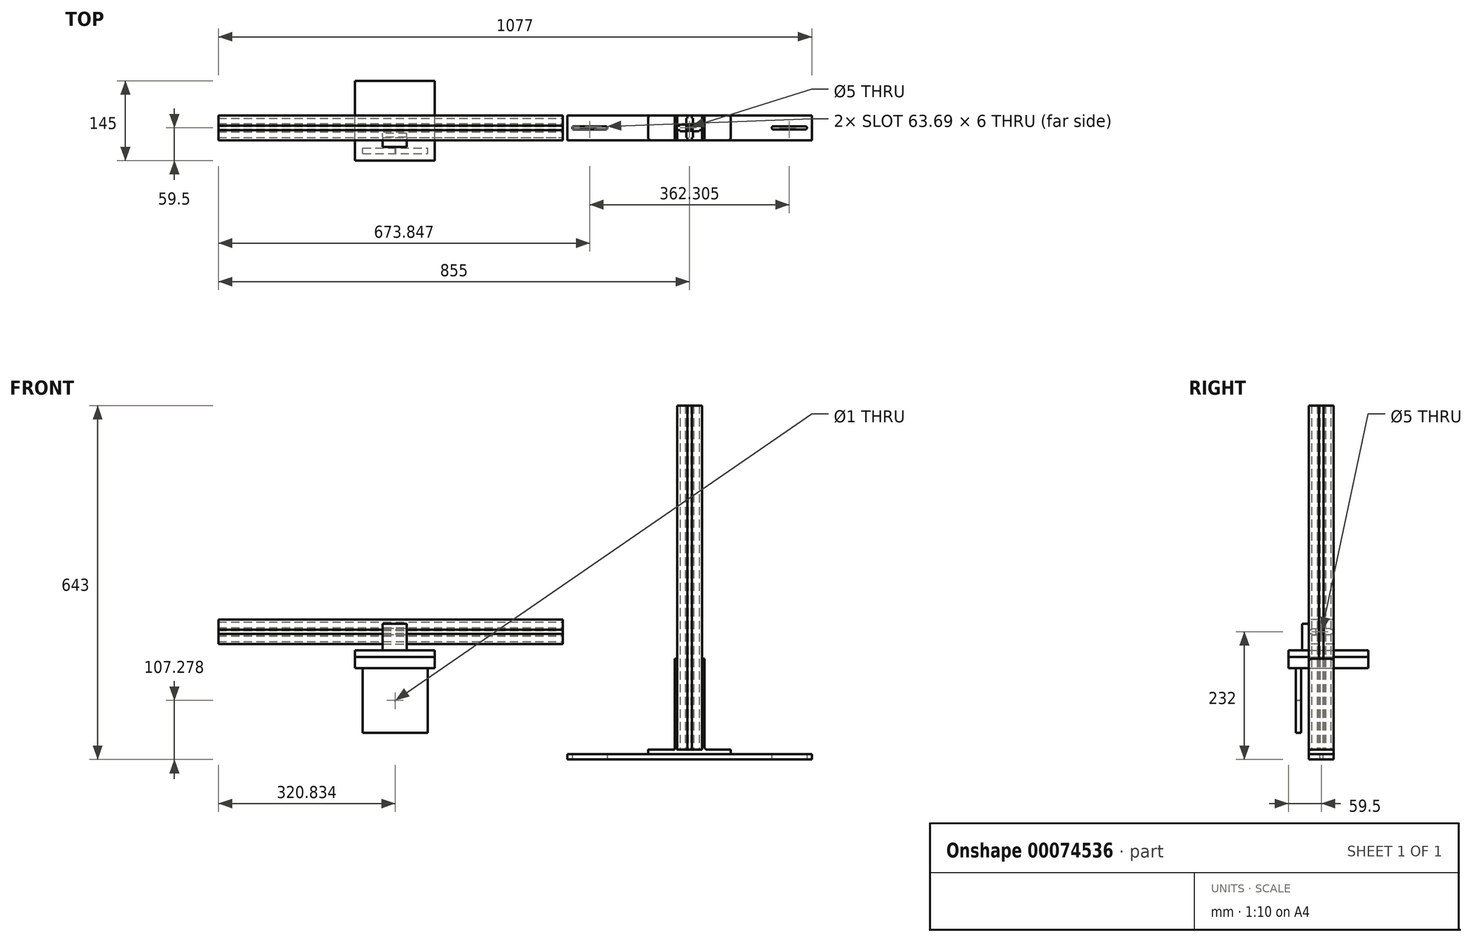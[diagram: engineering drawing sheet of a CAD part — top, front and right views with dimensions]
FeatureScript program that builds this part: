
annotation { "Feature Type Name" : "Feature", "Feature Type Description" : "" }
export const myFeature = defineFeature(function(context is Context, id is Id, definition is map)
    precondition{}
    {
        {
            var Q0;
            Q0=qCreatedBy(makeId("Top.planeOp"),FACE);
            var sketch = newSketch(context, id + "F0", { "sketchPlane" : qUnion([Q0])});
            skLineSegment(sketch, "E0.rect.bottom", {"start": v(-222, 22.5) * mm, "end": v(222, 22.5) * mm});
            skLineSegment(sketch, "E0.rect.top", {"start": v(-222, -22.5) * mm, "end": v(222, -22.5) * mm});
            skLineSegment(sketch, "E0.rect.left", {"start": v(-222, 22.5) * mm, "end": v(-222, -22.5) * mm});
            skLineSegment(sketch, "E0.rect.right", {"start": v(222, 22.5) * mm, "end": v(222, -22.5) * mm});
            skPoint(sketch, "E0.rect.middle", {"position": v(0, 0) * mm});
            skPoint(sketch, "E1", {"position": v(-210, 0) * mm});
            skPoint(sketch, "E2", {"position": v(-152.3, 0) * mm});
            skArc(sketch, "E3", {"start": v(-210, 3) * mm, "mid": v(-213, 0) * mm, "end": v(-210, -3) * mm});
            skArc(sketch, "E4", {"start": v(-152.3, 3) * mm, "mid": v(-149.3, 0) * mm, "end": v(-152.3, -3) * mm});
            skLineSegment(sketch, "E5", {"start": v(-210, -3) * mm, "end": v(-152.3, -3) * mm});
            skLineSegment(sketch, "E6", {"start": v(-210, 3) * mm, "end": v(-152.3, 3) * mm});
            skArc(sketch, "E7.MirrorCS", {"start": v(210, 3) * mm, "mid": v(213, 0) * mm, "end": v(210, -3) * mm});
            skLineSegment(sketch, "E8.MirrorCS", {"start": v(210, 3) * mm, "end": v(152.3, 3) * mm});
            skLineSegment(sketch, "E9.MirrorCS", {"start": v(210, -3) * mm, "end": v(152.3, -3) * mm});
            skArc(sketch, "E10.MirrorCS", {"start": v(152.3, 3) * mm, "mid": v(149.3, 0) * mm, "end": v(152.3, -3) * mm});
            skSolve(sketch);
        }
        {
            var Q0;
            Q0=makeQuery(id+"F0.imprint","IMPRINT",FACE,{"disambiguationData":[TD([[makeQuery(id+"F0.imprint","IMPRINT",EDGE,{"derivedFrom":sQuery(id+"F0.wireOp",EDGE,"E0.rect.bottom")}),-1.0]])]});
            extrude(context, id + "F1", {"entities" : qUnion([Q0]), "depth" : 10 * mm});
        }
        {
            var Q0;
            Q0=makeQuery(id+"F1.opExtrude","CAP_FACE",FACE,{"disambiguationData":[OSD([sQuery(id+"F0.wireOp",EDGE,"E0.rect.bottom"),sQuery(id+"F0.wireOp",EDGE,"E0.rect.top"),sQuery(id+"F0.wireOp",EDGE,"E0.rect.left"),sQuery(id+"F0.wireOp",EDGE,"E0.rect.right"),sQuery(id+"F0.wireOp",EDGE,"E3"),sQuery(id+"F0.wireOp",EDGE,"E4"),sQuery(id+"F0.wireOp",EDGE,"E5"),sQuery(id+"F0.wireOp",EDGE,"E6"),sQuery(id+"F0.wireOp",EDGE,"E7.MirrorCS"),sQuery(id+"F0.wireOp",EDGE,"E8.MirrorCS"),sQuery(id+"F0.wireOp",EDGE,"E9.MirrorCS"),sQuery(id+"F0.wireOp",EDGE,"E10.MirrorCS")])],"isStart":false});
            var sketch = newSketch(context, id + "F2", { "sketchPlane" : qUnion([Q0])});
            skLineSegment(sketch, "E11.rect.bottom", {"start": v(75, 22.5) * mm, "end": v(-75, 22.5) * mm});
            skLineSegment(sketch, "E11.rect.top", {"start": v(75, -22.5) * mm, "end": v(-75, -22.5) * mm});
            skLineSegment(sketch, "E11.rect.left", {"start": v(75, 22.5) * mm, "end": v(75, -22.5) * mm});
            skLineSegment(sketch, "E11.rect.right", {"start": v(-75, 22.5) * mm, "end": v(-75, -22.5) * mm});
            skPoint(sketch, "E11.rect.middle", {"position": v(0, 0) * mm});
            skSolve(sketch);
        }
        {
            var Q0;
            Q0=makeQuery(id+"F2.imprint","IMPRINT",FACE,{"disambiguationData":[TD([[makeQuery(id+"F2.imprint","IMPRINT",EDGE,{"derivedFrom":sQuery(id+"F2.wireOp",EDGE,"E11.rect.bottom")}),-1.0]])]});
            extrude(context, id + "F3", {"entities" : qUnion([Q0]), "depth" : 8 * mm});
        }
        {
            var Q0;
            Q0=makeQuery(id+"F3.opExtrude","SWEPT_EDGE",EDGE,{"disambiguationData":[OSD([sQuery(id+"F0.wireOp",EDGE,"E0.rect.top"),sQuery(id+"F2.wireOp",EDGE,"E11.rect.top"),sQuery(id+"F2.wireOp",EDGE,"E11.rect.right")])]});
            var Q1;
            Q1=makeQuery(id+"F3.opExtrude","SWEPT_EDGE",EDGE,{"disambiguationData":[OSD([sQuery(id+"F0.wireOp",EDGE,"E0.rect.bottom"),sQuery(id+"F2.wireOp",EDGE,"E11.rect.bottom"),sQuery(id+"F2.wireOp",EDGE,"E11.rect.right")])]});
            var Q2;
            Q2=makeQuery(id+"F3.opExtrude","SWEPT_EDGE",EDGE,{"disambiguationData":[OSD([sQuery(id+"F0.wireOp",EDGE,"E0.rect.top"),sQuery(id+"F2.wireOp",EDGE,"E11.rect.top"),sQuery(id+"F2.wireOp",EDGE,"E11.rect.left")])]});
            var Q3;
            Q3=makeQuery(id+"F3.opExtrude","SWEPT_EDGE",EDGE,{"disambiguationData":[OSD([sQuery(id+"F0.wireOp",EDGE,"E0.rect.bottom"),sQuery(id+"F2.wireOp",EDGE,"E11.rect.bottom"),sQuery(id+"F2.wireOp",EDGE,"E11.rect.left")])]});
            fillet(context, id + "F4", {"entities" : qUnion([Q0, Q1, Q2, Q3]), "radius" : 5 * mm, "tangentPropagation" : true, "allowEdgeOverflow" : false});
        }
        {
            var Q0;
            Q0=makeQuery(id+"F3.opExtrude","CAP_FACE",FACE,{"disambiguationData":[OSD([sQuery(id+"F2.wireOp",EDGE,"E11.rect.bottom"),sQuery(id+"F2.wireOp",EDGE,"E11.rect.top"),sQuery(id+"F2.wireOp",EDGE,"E11.rect.left"),sQuery(id+"F2.wireOp",EDGE,"E11.rect.right")])],"isStart":false});
            var sketch = newSketch(context, id + "F5", { "sketchPlane" : qUnion([Q0])});
            skLineSegment(sketch, "E12.rect.bottom", {"start": v(-23, 22.5) * mm, "end": v(-27, 22.5) * mm});
            skLineSegment(sketch, "E12.rect.top", {"start": v(-23, -22.5) * mm, "end": v(-27, -22.5) * mm});
            skLineSegment(sketch, "E12.rect.left", {"start": v(-23, 22.5) * mm, "end": v(-23, -22.5) * mm});
            skLineSegment(sketch, "E12.rect.right", {"start": v(-27, 22.5) * mm, "end": v(-27, -22.5) * mm});
            skPoint(sketch, "E12.rect.middle", {"position": v(-25, 0) * mm});
            skLineSegment(sketch, "E13.MirrorCS", {"start": v(23, 22.5) * mm, "end": v(23, -22.5) * mm});
            skLineSegment(sketch, "E14.MirrorCS", {"start": v(23, 22.5) * mm, "end": v(27, 22.5) * mm});
            skLineSegment(sketch, "E15.MirrorCS", {"start": v(27, 22.5) * mm, "end": v(27, -22.5) * mm});
            skLineSegment(sketch, "E16.MirrorCS", {"start": v(23, -22.5) * mm, "end": v(27, -22.5) * mm});
            skSolve(sketch);
        }
        {
            var Q0;
            Q0=makeQuery(id+"F5.imprint","IMPRINT",FACE,{"disambiguationData":[TD([[makeQuery(id+"F5.imprint","IMPRINT",EDGE,{"derivedFrom":sQuery(id+"F5.wireOp",EDGE,"E12.rect.bottom")}),-1.0]])]});
            var Q1;
            Q1=makeQuery(id+"F5.imprint","IMPRINT",FACE,{"disambiguationData":[TD([[makeQuery(id+"F5.imprint","IMPRINT",EDGE,{"derivedFrom":sQuery(id+"F5.wireOp",EDGE,"E13.MirrorCS")}),1.0]])]});
            extrude(context, id + "F6", {"entities" : qUnion([Q0, Q1]), "operationType" : NewBodyOperationType.ADD, "depth" : 165 * mm});
        }
        {
            var Q0;
            Q0=makeQuery(id+"F6.opExtrude","CAP_EDGE",EDGE,{"disambiguationData":[OSD([sQuery(id+"F5.wireOp",EDGE,"E16.MirrorCS")])],"isStart":false});
            var Q1;
            Q1=makeQuery(id+"F6.opExtrude","CAP_EDGE",EDGE,{"disambiguationData":[OSD([sQuery(id+"F5.wireOp",EDGE,"E12.rect.top")])],"isStart":false});
            var Q2;
            Q2=makeQuery(id+"F6.opExtrude","CAP_EDGE",EDGE,{"disambiguationData":[OSD([sQuery(id+"F5.wireOp",EDGE,"E12.rect.bottom")])],"isStart":false});
            var Q3;
            Q3=makeQuery(id+"F6.opExtrude","CAP_EDGE",EDGE,{"disambiguationData":[OSD([sQuery(id+"F5.wireOp",EDGE,"E14.MirrorCS")])],"isStart":false});
            fillet(context, id + "F7", {"entities" : qUnion([Q0, Q1, Q2, Q3]), "radius" : 5 * mm, "tangentPropagation" : true, "allowEdgeOverflow" : false});
        }
        {
            var Q0;
            Q0=makeQuery(id+"F6.opExtrude","CAP_EDGE",EDGE,{"disambiguationData":[OSD([sQuery(id+"F5.wireOp",EDGE,"E12.rect.right")])],"isStart":true});
            var Q1;
            Q1=makeQuery(id+"F6.opExtrude","CAP_EDGE",EDGE,{"disambiguationData":[OSD([sQuery(id+"F5.wireOp",EDGE,"E15.MirrorCS")])],"isStart":true});
            fillet(context, id + "F8", {"entities" : qUnion([Q0, Q1]), "radius" : 5 * mm, "tangentPropagation" : true, "allowEdgeOverflow" : false});
        }
        {
            var Q0;
            {var subQ0=sQuery(id+"F2.wireOp",EDGE,"E11.rect.top");var subQ1=sQuery(id+"F2.wireOp",EDGE,"E11.rect.bottom");Q0=makeQuery(id+"F6.boolean.opBoolean","SPLIT",FACE,{"disambiguationData":[TD([makeQuery(id+"F6.opExtrude","SWEPT_FACE",FACE,{"disambiguationData":[OSD([sQuery(id+"F5.wireOp",EDGE,"E12.rect.left")])]})])],"derivedFrom":makeQuery(id+"F3.opExtrude","CAP_FACE",FACE,{"disambiguationData":[OSD([subQ1,subQ0,sQuery(id+"F2.wireOp",EDGE,"E11.rect.left"),sQuery(id+"F2.wireOp",EDGE,"E11.rect.right")])],"isStart":false})});}
            var sketch = newSketch(context, id + "F9", { "sketchPlane" : qUnion([Q0])});
            skLineSegment(sketch, "E17.rect.bottom", {"start": v(22.5, 22.5) * mm, "end": v(-22.5, 22.5) * mm});
            skLineSegment(sketch, "E17.rect.top", {"start": v(22.5, -22.5) * mm, "end": v(-22.5, -22.5) * mm});
            skLineSegment(sketch, "E17.rect.left", {"start": v(22.5, 22.5) * mm, "end": v(22.5, -22.5) * mm});
            skLineSegment(sketch, "E17.rect.right", {"start": v(-22.5, 22.5) * mm, "end": v(-22.5, -22.5) * mm});
            skPoint(sketch, "E17.rect.middle", {"position": v(0, 0) * mm});
            skLineSegment(sketch, "E18", {"start": v(4, 22.5) * mm, "end": v(4, 17.5) * mm});
            skLineSegment(sketch, "E19", {"start": v(4, 17.5) * mm, "end": v(6, 17.5) * mm});
            skLineSegment(sketch, "E20", {"start": v(6, 17.5) * mm, "end": v(6, 7.5) * mm});
            skLineSegment(sketch, "E21", {"start": v(6, 7.5) * mm, "end": v(4.33, 5.58) * mm});
            skLineSegment(sketch, "E22", {"start": v(4.33, 5.58) * mm, "end": v(0, 5.58) * mm});
            skLineSegment(sketch, "E23", {"start": v(0, 5.58) * mm, "end": v(0, 22.5) * mm});
            skLineSegment(sketch, "E24", {"start": v(0, 22.5) * mm, "end": v(4, 22.5) * mm});
            skLineSegment(sketch, "E25.MirrorCS", {"start": v(0, 22.5) * mm, "end": v(-4, 22.5) * mm});
            skLineSegment(sketch, "E26.MirrorCS", {"start": v(-4, 22.5) * mm, "end": v(-4, 17.5) * mm});
            skLineSegment(sketch, "E27.MirrorCS", {"start": v(-4, 17.5) * mm, "end": v(-6, 17.5) * mm});
            skLineSegment(sketch, "E28.MirrorCS", {"start": v(-6, 17.5) * mm, "end": v(-6, 7.5) * mm});
            skLineSegment(sketch, "E29.MirrorCS", {"start": v(-6, 7.5) * mm, "end": v(-4.33, 5.58) * mm});
            skLineSegment(sketch, "E30.MirrorCS", {"start": v(-4.33, 5.58) * mm, "end": v(0, 5.58) * mm});
            skLineSegment(sketch, "E31.MirrorCS", {"start": v(0, -22.5) * mm, "end": v(4, -22.5) * mm});
            skLineSegment(sketch, "E32.1.0", {"start": v(-22.5, 0) * mm, "end": v(-22.5, -4) * mm});
            skLineSegment(sketch, "E32.1.1", {"start": v(-22.5, 0) * mm, "end": v(-22.5, 4) * mm});
            skLineSegment(sketch, "E32.1.2", {"start": v(-22.5, 4) * mm, "end": v(-17.5, 4) * mm});
            skLineSegment(sketch, "E32.1.3", {"start": v(-17.5, 4) * mm, "end": v(-17.5, 6) * mm});
            skLineSegment(sketch, "E32.1.4", {"start": v(-17.5, 6) * mm, "end": v(-7.5, 6) * mm});
            skLineSegment(sketch, "E32.1.5", {"start": v(-7.5, 6) * mm, "end": v(-5.58, 4.33) * mm});
            skLineSegment(sketch, "E32.1.6", {"start": v(-5.58, 4.33) * mm, "end": v(-5.58, 0) * mm});
            skLineSegment(sketch, "E32.1.7", {"start": v(-5.58, -4.33) * mm, "end": v(-5.58, 0) * mm});
            skLineSegment(sketch, "E32.1.8", {"start": v(-7.5, -6) * mm, "end": v(-5.58, -4.33) * mm});
            skLineSegment(sketch, "E32.1.9", {"start": v(-17.5, -6) * mm, "end": v(-7.5, -6) * mm});
            skLineSegment(sketch, "E32.1.10", {"start": v(-17.5, -4) * mm, "end": v(-17.5, -6) * mm});
            skLineSegment(sketch, "E32.1.11", {"start": v(-22.5, -4) * mm, "end": v(-17.5, -4) * mm});
            skLineSegment(sketch, "E32.2.1", {"start": v(0, -22.5) * mm, "end": v(-4, -22.5) * mm});
            skLineSegment(sketch, "E32.2.2", {"start": v(-4, -22.5) * mm, "end": v(-4, -17.5) * mm});
            skLineSegment(sketch, "E32.2.3", {"start": v(-4, -17.5) * mm, "end": v(-6, -17.5) * mm});
            skLineSegment(sketch, "E32.2.4", {"start": v(-6, -17.5) * mm, "end": v(-6, -7.5) * mm});
            skLineSegment(sketch, "E32.2.5", {"start": v(-6, -7.5) * mm, "end": v(-4.33, -5.58) * mm});
            skLineSegment(sketch, "E32.2.6", {"start": v(-4.33, -5.58) * mm, "end": v(0, -5.58) * mm});
            skLineSegment(sketch, "E32.2.7", {"start": v(4.33, -5.58) * mm, "end": v(0, -5.58) * mm});
            skLineSegment(sketch, "E32.2.8", {"start": v(6, -7.5) * mm, "end": v(4.33, -5.58) * mm});
            skLineSegment(sketch, "E32.2.9", {"start": v(6, -17.5) * mm, "end": v(6, -7.5) * mm});
            skLineSegment(sketch, "E32.2.10", {"start": v(4, -17.5) * mm, "end": v(6, -17.5) * mm});
            skLineSegment(sketch, "E32.2.11", {"start": v(4, -22.5) * mm, "end": v(4, -17.5) * mm});
            skLineSegment(sketch, "E32.3.0", {"start": v(22.5, 0) * mm, "end": v(22.5, 4) * mm});
            skLineSegment(sketch, "E32.3.1", {"start": v(22.5, 0) * mm, "end": v(22.5, -4) * mm});
            skLineSegment(sketch, "E32.3.2", {"start": v(22.5, -4) * mm, "end": v(17.5, -4) * mm});
            skLineSegment(sketch, "E32.3.3", {"start": v(17.5, -4) * mm, "end": v(17.5, -6) * mm});
            skLineSegment(sketch, "E32.3.4", {"start": v(17.5, -6) * mm, "end": v(7.5, -6) * mm});
            skLineSegment(sketch, "E32.3.5", {"start": v(7.5, -6) * mm, "end": v(5.58, -4.33) * mm});
            skLineSegment(sketch, "E32.3.6", {"start": v(5.58, -4.33) * mm, "end": v(5.58, 0) * mm});
            skLineSegment(sketch, "E32.3.7", {"start": v(5.58, 4.33) * mm, "end": v(5.58, 0) * mm});
            skLineSegment(sketch, "E32.3.8", {"start": v(7.5, 6) * mm, "end": v(5.58, 4.33) * mm});
            skLineSegment(sketch, "E32.3.9", {"start": v(17.5, 6) * mm, "end": v(7.5, 6) * mm});
            skLineSegment(sketch, "E32.3.10", {"start": v(17.5, 4) * mm, "end": v(17.5, 6) * mm});
            skLineSegment(sketch, "E32.3.11", {"start": v(22.5, 4) * mm, "end": v(17.5, 4) * mm});
            skCircle(sketch, "E33", {"center": v(0, 0) * mm, "radius": 2.5 * mm});
            skSolve(sketch);
        }
        {
            var Q0;
            {var subQ22=sQuery(id+"F9.wireOp",EDGE,"E18");Q0=makeQuery(id+"F9.imprint","IMPRINT",FACE,{"disambiguationData":[TD([[makeQuery(id+"F9.imprint","IMPRINT",EDGE,{"derivedFrom":subQ22}),1.0]])]});}
            extrude(context, id + "F10", {"entities" : qUnion([Q0]), "depth" : 625 * mm});
        }
        {
            var Q0;
            Q0=makeQuery(id+"F10.opExtrude","SWEPT_BODY",BODY,{"disambiguationData":[OSD([sQuery(id+"F9.wireOp",EDGE,"E17.rect.bottom"),sQuery(id+"F9.wireOp",EDGE,"E17.rect.top"),sQuery(id+"F9.wireOp",EDGE,"E17.rect.left"),sQuery(id+"F9.wireOp",EDGE,"E17.rect.right"),sQuery(id+"F9.wireOp",EDGE,"E18"),sQuery(id+"F9.wireOp",EDGE,"E19"),sQuery(id+"F9.wireOp",EDGE,"E20"),sQuery(id+"F9.wireOp",EDGE,"E21"),sQuery(id+"F9.wireOp",EDGE,"E22"),sQuery(id+"F9.wireOp",EDGE,"E26.MirrorCS"),sQuery(id+"F9.wireOp",EDGE,"E27.MirrorCS"),sQuery(id+"F9.wireOp",EDGE,"E28.MirrorCS"),sQuery(id+"F9.wireOp",EDGE,"E29.MirrorCS"),sQuery(id+"F9.wireOp",EDGE,"E30.MirrorCS"),sQuery(id+"F9.wireOp",EDGE,"E32.1.2"),sQuery(id+"F9.wireOp",EDGE,"E32.1.3"),sQuery(id+"F9.wireOp",EDGE,"E32.1.4"),sQuery(id+"F9.wireOp",EDGE,"E32.1.5"),sQuery(id+"F9.wireOp",EDGE,"E32.1.6"),sQuery(id+"F9.wireOp",EDGE,"E32.1.7"),sQuery(id+"F9.wireOp",EDGE,"E32.1.8"),sQuery(id+"F9.wireOp",EDGE,"E32.1.9"),sQuery(id+"F9.wireOp",EDGE,"E32.1.10"),sQuery(id+"F9.wireOp",EDGE,"E32.1.11"),sQuery(id+"F9.wireOp",EDGE,"E32.2.2"),sQuery(id+"F9.wireOp",EDGE,"E32.2.3"),sQuery(id+"F9.wireOp",EDGE,"E32.2.4"),sQuery(id+"F9.wireOp",EDGE,"E32.2.5"),sQuery(id+"F9.wireOp",EDGE,"E32.2.6"),sQuery(id+"F9.wireOp",EDGE,"E32.2.7"),sQuery(id+"F9.wireOp",EDGE,"E32.2.8"),sQuery(id+"F9.wireOp",EDGE,"E32.2.9"),sQuery(id+"F9.wireOp",EDGE,"E32.2.10"),sQuery(id+"F9.wireOp",EDGE,"E32.2.11"),sQuery(id+"F9.wireOp",EDGE,"E32.3.2"),sQuery(id+"F9.wireOp",EDGE,"E32.3.3"),sQuery(id+"F9.wireOp",EDGE,"E32.3.4"),sQuery(id+"F9.wireOp",EDGE,"E32.3.5"),sQuery(id+"F9.wireOp",EDGE,"E32.3.6"),sQuery(id+"F9.wireOp",EDGE,"E32.3.7"),sQuery(id+"F9.wireOp",EDGE,"E32.3.8"),sQuery(id+"F9.wireOp",EDGE,"E32.3.9"),sQuery(id+"F9.wireOp",EDGE,"E32.3.10"),sQuery(id+"F9.wireOp",EDGE,"E32.3.11"),sQuery(id+"F9.wireOp",EDGE,"E33")])]});
            var Q1;
            Q1=makeQuery(id+"F1.opExtrude","CAP_EDGE",EDGE,{"disambiguationData":[OSD([sQuery(id+"F0.wireOp",EDGE,"E0.rect.left")])],"isStart":false});
            transform(context, id + "F11", {"entities" : qUnion([Q0]), "transformType" : TransformType.ROTATION, "transformAxis" : qUnion([Q1]), "angle" : 90 * degree, "makeCopy" : true});
        }
        {
            var Q0;
            {var subQ0=sQuery(id+"F9.wireOp",EDGE,"E17.rect.top");Q0=makeQuery(id+"F11.opPattern","COPY",FACE,{"derivedFrom":makeQuery(id+"F10.opExtrude","SWEPT_FACE",FACE,{"disambiguationData":[OSD([subQ0]),TDD([makeQuery(id+"F9.imprint","IMPRINT",EDGE,{"disambiguationData":[TD([[makeQuery(id+"F9.imprint","INTERSECT",VERTEX,{"derivedFrom":[subQ0,sQuery(id+"F9.wireOp",EDGE,"E31.MirrorCS"),sQuery(id+"F9.wireOp",EDGE,"E32.2.11")]}),-1.0]])],"derivedFrom":subQ0})])]}),"instanceName":"1"});}
            var sketch = newSketch(context, id + "F12", { "sketchPlane" : qUnion([Q0])});
            skLineSegment(sketch, "E34.bottom", {"start": v(-557.17, 246.92) * mm, "end": v(-513.53, 246.92) * mm});
            skLineSegment(sketch, "E34.top", {"start": v(-557.17, 198.28) * mm, "end": v(-513.53, 198.28) * mm});
            skLineSegment(sketch, "E34.left", {"start": v(-557.17, 246.92) * mm, "end": v(-557.17, 198.28) * mm});
            skLineSegment(sketch, "E34.right", {"start": v(-513.53, 246.92) * mm, "end": v(-513.53, 198.28) * mm});
            skSolve(sketch);
        }
        {
            var Q0;
            {var subQ0=sQuery(id+"F12.wireOp",EDGE,"E34.top");Q0=makeQuery(id+"F12.imprint","IMPRINT",FACE,{"disambiguationData":[TD([[makeQuery(id+"F12.imprint","IMPRINT",EDGE,{"derivedFrom":subQ0}),1.0]])]});}
            var Q1;
            {var subQ0=sQuery(id+"F12.wireOp",EDGE,"E34.bottom");Q1=makeQuery(id+"F12.imprint","IMPRINT",FACE,{"disambiguationData":[TD([[makeQuery(id+"F12.imprint","IMPRINT",EDGE,{"derivedFrom":subQ0}),-1.0]])]});}
            extrude(context, id + "F13", {"entities" : qUnion([Q0, Q1]), "depth" : 12 * mm});
        }
        {
            var Q0;
            Q0=makeQuery(id+"F13.opExtrude","SWEPT_FACE",FACE,{"disambiguationData":[OSD([sQuery(id+"F12.wireOp",EDGE,"E34.left")])]});
            var sketch = newSketch(context, id + "F14", { "sketchPlane" : qUnion([Q0])});
            skLineSegment(sketch, "E35", {"start": v(22.5, 236) * mm, "end": v(16.98, 236) * mm});
            skLineSegment(sketch, "E36", {"start": v(16.98, 236) * mm, "end": v(16.98, 238) * mm});
            skLineSegment(sketch, "E37", {"start": v(16.98, 238) * mm, "end": v(10.23, 238) * mm});
            skLineSegment(sketch, "E38", {"start": v(10.23, 238) * mm, "end": v(10.23, 226.55) * mm});
            skLineSegment(sketch, "E39", {"start": v(10.23, 226.55) * mm, "end": v(16.98, 226.55) * mm});
            skLineSegment(sketch, "E40", {"start": v(16.98, 226.55) * mm, "end": v(16.98, 228) * mm});
            skLineSegment(sketch, "E41", {"start": v(16.98, 228) * mm, "end": v(22.5, 228) * mm});
            skLineSegment(sketch, "E42", {"start": v(22.5, 228) * mm, "end": v(22.5, 236) * mm});
            skSolve(sketch);
        }
        {
            var Q0;
            Q0=makeQuery(id+"F14.imprint","IMPRINT",FACE,{"disambiguationData":[TD([[makeQuery(id+"F14.imprint","IMPRINT",EDGE,{"derivedFrom":sQuery(id+"F14.wireOp",EDGE,"E35")}),1.0]])]});
            var Q1;
            Q1=makeQuery(id+"F13.opExtrude","SWEPT_FACE",FACE,{"disambiguationData":[OSD([sQuery(id+"F12.wireOp",EDGE,"E34.right")])]});
            extrude(context, id + "F15", {"entities" : qUnion([Q0]), "operationType" : NewBodyOperationType.ADD, "endBound" : BoundingType.UP_TO_SURFACE, "oppositeDirection" : true, "endBoundEntityFace" : qUnion([Q1]), "depth" : 25 * mm});
        }
        {
            var Q0;
            Q0=makeQuery(id+"F13.opExtrude","SWEPT_FACE",FACE,{"disambiguationData":[OSD([sQuery(id+"F12.wireOp",EDGE,"E34.top")])]});
            var sketch = newSketch(context, id + "F16", { "sketchPlane" : qUnion([Q0])});
            skLineSegment(sketch, "E43.bottom", {"start": v(-607.17, 59.5) * mm, "end": v(-462.17, 59.5) * mm});
            skLineSegment(sketch, "E43.top", {"start": v(-607.17, -85.5) * mm, "end": v(-462.17, -85.5) * mm});
            skLineSegment(sketch, "E43.left", {"start": v(-607.17, 59.5) * mm, "end": v(-607.17, -85.5) * mm});
            skLineSegment(sketch, "E43.right", {"start": v(-462.17, 59.5) * mm, "end": v(-462.17, -85.5) * mm});
            skSolve(sketch);
        }
        {
            var Q0;
            Q0=makeQuery(id+"F16.imprint","IMPRINT",FACE,{"disambiguationData":[TD([[makeQuery(id+"F16.imprint","IMPRINT",EDGE,{"derivedFrom":sQuery(id+"F16.wireOp",EDGE,"E43.bottom")}),-1.0]])]});
            var Q1;
            {var subQ0=sQuery(id+"F12.wireOp",EDGE,"E34.top");Q1=makeQuery(id+"F16.imprint","IMPRINT",FACE,{"disambiguationData":[TD([[makeQuery(id+"F16.imprint","IMPRINT",EDGE,{"derivedFrom":makeQuery(id+"F13.opExtrude","CAP_EDGE",EDGE,{"disambiguationData":[OSD([subQ0])],"isStart":true})}),1.0]])]});}
            extrude(context, id + "F17", {"entities" : qUnion([Q0, Q1]), "operationType" : NewBodyOperationType.ADD, "depth" : 12 * mm});
        }
        {
            var Q0;
            Q0=makeQuery(id+"F17.opExtrude","CAP_FACE",FACE,{"disambiguationData":[OSD([sQuery(id+"F16.wireOp",EDGE,"E43.bottom"),sQuery(id+"F16.wireOp",EDGE,"E43.top"),sQuery(id+"F16.wireOp",EDGE,"E43.left"),sQuery(id+"F16.wireOp",EDGE,"E43.right")])],"isStart":false});
            extrude(context, id + "F18", {"entities" : qUnion([Q0]), "depth" : 20 * mm});
        }
        {
            var Q0;
            Q0=makeQuery(id+"F18.opExtrude","CAP_FACE",FACE,{"disambiguationData":[OSD([sQuery(id+"F16.wireOp",EDGE,"E43.bottom"),sQuery(id+"F16.wireOp",EDGE,"E43.top"),sQuery(id+"F16.wireOp",EDGE,"E43.left"),sQuery(id+"F16.wireOp",EDGE,"E43.right")])],"isStart":false});
            var sketch = newSketch(context, id + "F19", { "sketchPlane" : qUnion([Q0])});
            skLineSegment(sketch, "E44.bottom", {"start": v(-593.17, 46.5) * mm, "end": v(-475.17, 46.5) * mm});
            skLineSegment(sketch, "E44.top", {"start": v(-593.17, 36.5) * mm, "end": v(-475.17, 36.5) * mm});
            skLineSegment(sketch, "E44.left", {"start": v(-593.17, 46.5) * mm, "end": v(-593.17, 36.5) * mm});
            skLineSegment(sketch, "E44.right", {"start": v(-475.17, 46.5) * mm, "end": v(-475.17, 36.5) * mm});
            skSolve(sketch);
        }
        {
            var Q0;
            Q0=makeQuery(id+"F19.imprint","IMPRINT",FACE,{"disambiguationData":[TD([[makeQuery(id+"F19.imprint","IMPRINT",EDGE,{"derivedFrom":sQuery(id+"F19.wireOp",EDGE,"E44.bottom")}),-1.0]])]});
            extrude(context, id + "F20", {"entities" : qUnion([Q0]), "depth" : 118 * mm});
        }
        {
            var Q0;
            Q0=makeQuery(id+"F20.opExtrude","SWEPT_FACE",FACE,{"disambiguationData":[OSD([sQuery(id+"F19.wireOp",EDGE,"E44.bottom")])]});
            var sketch = newSketch(context, id + "F21", { "sketchPlane" : qUnion([Q0])});
            skLineSegment(sketch, "E45", {"start": v(-593.17, 166.28) * mm, "end": v(-475.17, 48.28) * mm, "construction": true});
            skLineSegment(sketch, "E46", {"start": v(-593.17, 48.28) * mm, "end": v(-475.17, 166.28) * mm, "construction": true});
            skCircle(sketch, "E47", {"center": v(-534.17, 107.28) * mm, "radius": 0.5 * mm});
            skSolve(sketch);
        }
        {
            var Q0;
            Q0=makeQuery(id+"F21.imprint","IMPRINT",FACE,{"disambiguationData":[TD([[makeQuery(id+"F21.imprint","IMPRINT",EDGE,{"derivedFrom":sQuery(id+"F21.wireOp",EDGE,"E47")}),1.0]])]});
            extrude(context, id + "F22", {"entities" : qUnion([Q0]), "operationType" : NewBodyOperationType.REMOVE, "oppositeDirection" : true, "depth" : 25 * mm});
        }
    });
